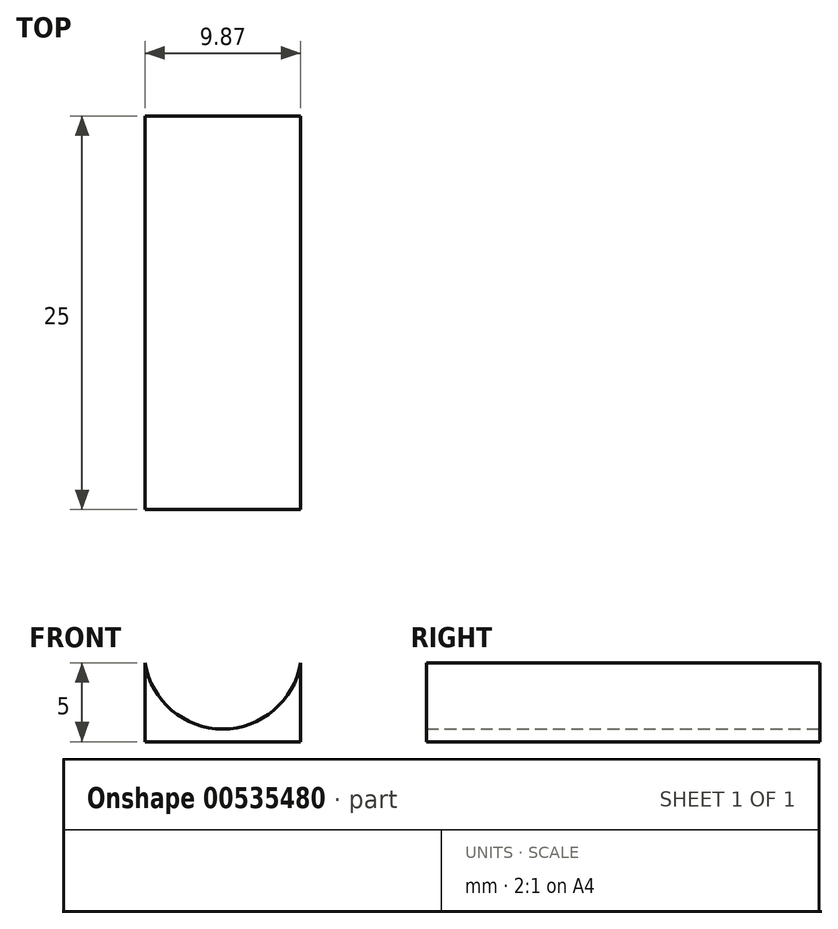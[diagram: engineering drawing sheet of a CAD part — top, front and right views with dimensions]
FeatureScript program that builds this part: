
annotation { "Feature Type Name" : "Feature", "Feature Type Description" : "" }
export const myFeature = defineFeature(function(context is Context, id is Id, definition is map)
    precondition{}
    {
        {
            var Q0;
            Q0=qCreatedBy(makeId("Front.planeOp"),FACE);
            var sketch = newSketch(context, id + "F0", { "sketchPlane" : qUnion([Q0])});
            skArc(sketch, "E0", {"start": v(0, -1.61) * mm, "mid": v(4.93, -5.8) * mm, "end": v(9.87, -1.61) * mm});
            skLineSegment(sketch, "E1.top", {"start": v(0, -6.61) * mm, "end": v(9.87, -6.61) * mm});
            skLineSegment(sketch, "E1.left", {"start": v(0, -1.61) * mm, "end": v(0, -6.61) * mm});
            skLineSegment(sketch, "E1.right", {"start": v(9.87, -1.61) * mm, "end": v(9.87, -6.61) * mm});
            skPoint(sketch, "E2.orphan", {"position": v(0, 0) * mm});
            skSolve(sketch);
        }
        {
            var Q0;
            Q0 = qSketchRegion(id + "F0", true);
            extrude(context, id + "F1", {"entities" : qUnion([Q0]), "depth" : 25 * mm, "offsetDistance" : 25 * mm});
        }
    });
